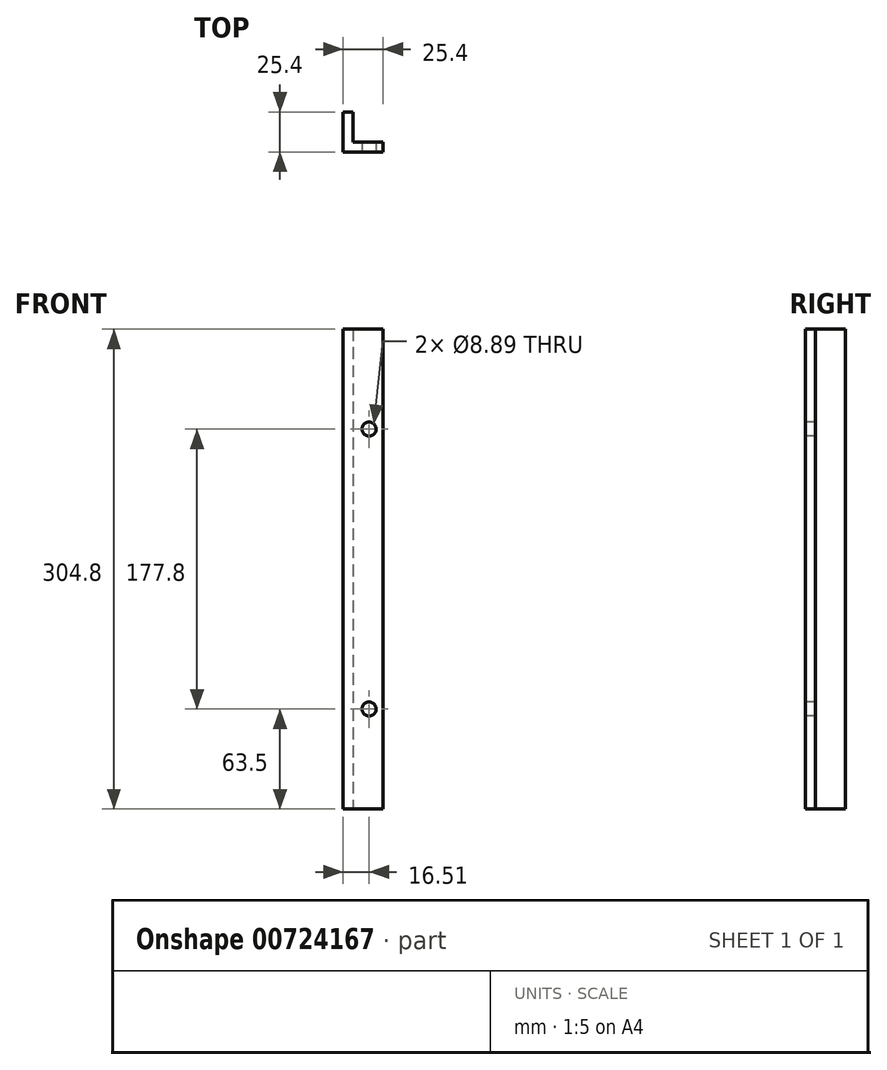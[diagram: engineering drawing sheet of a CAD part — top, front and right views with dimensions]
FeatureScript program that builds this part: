
annotation { "Feature Type Name" : "Feature", "Feature Type Description" : "" }
export const myFeature = defineFeature(function(context is Context, id is Id, definition is map)
    precondition{}
    {
        {
            var Q0;
            Q0=qCreatedBy(makeId("Top.planeOp"),FACE);
            var sketch = newSketch(context, id + "F0", { "sketchPlane" : qUnion([Q0])});
            skLineSegment(sketch, "E0", {"start": v(0, 0) * mm, "end": v(-25.4, 0) * mm});
            skLineSegment(sketch, "E1", {"start": v(-25.4, 0) * mm, "end": v(-25.4, 25.4) * mm});
            skLineSegment(sketch, "E2", {"start": v(-25.4, 25.4) * mm, "end": v(-19.05, 25.4) * mm});
            skLineSegment(sketch, "E3", {"start": v(-19.05, 25.4) * mm, "end": v(-19.05, 6.35) * mm});
            skLineSegment(sketch, "E4", {"start": v(-19.05, 6.35) * mm, "end": v(0, 6.35) * mm});
            skLineSegment(sketch, "E5", {"start": v(0, 6.35) * mm, "end": v(0, 0) * mm});
            skSolve(sketch);
        }
        {
            var Q0;
            Q0=makeQuery(id+"F0.imprint","IMPRINT",FACE,{"disambiguationData":[TD([[makeQuery(id+"F0.imprint","IMPRINT",EDGE,{"derivedFrom":sQuery(id+"F0.wireOp",EDGE,"E0")}),-1.0]])]});
            extrude(context, id + "F1", {"entities" : qUnion([Q0]), "depth" : 304.8 * mm, "offsetDistance" : 25.4 * mm, "symmetric" : true});
        }
        {
            var Q0;
            Q0=makeQuery(id+"F1.opExtrude","SWEPT_FACE",FACE,{"disambiguationData":[OSD([sQuery(id+"F0.wireOp",EDGE,"E0")])]});
            var sketch = newSketch(context, id + "F2", { "sketchPlane" : qUnion([Q0])});
            skLineSegment(sketch, "E6", {"start": v(0, 0) * mm, "end": v(-8.89, 0) * mm, "construction": true});
            skLineSegment(sketch, "E7", {"start": v(-8.89, 0) * mm, "end": v(-8.89, 88.9) * mm, "construction": true});
            skLineSegment(sketch, "E8", {"start": v(-8.89, 0) * mm, "end": v(-8.89, -88.9) * mm, "construction": true});
            skCircle(sketch, "E9", {"center": v(-8.89, 88.9) * mm, "radius": 4.45 * mm});
            skCircle(sketch, "E10", {"center": v(-8.89, -88.9) * mm, "radius": 4.45 * mm});
            skSolve(sketch);
        }
        {
            var Q0;
            Q0 = qSketchRegion(id + "F2", true);
            extrude(context, id + "F3", {"entities" : qUnion([Q0]), "operationType" : NewBodyOperationType.REMOVE, "oppositeDirection" : true, "depth" : 25.4 * mm, "offsetDistance" : 25.4 * mm});
        }
    });
